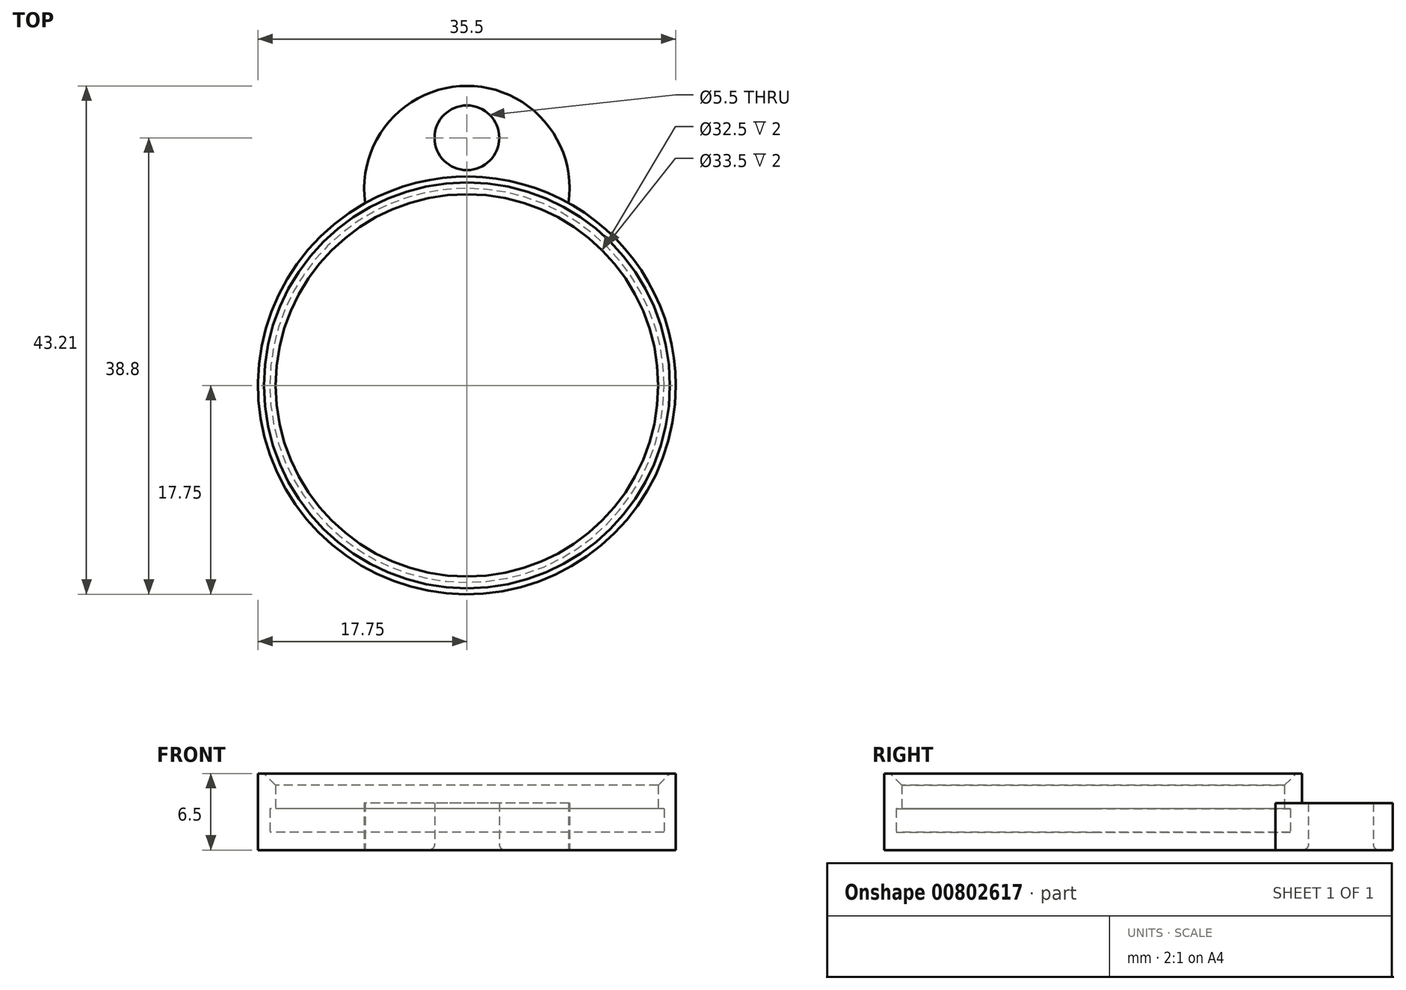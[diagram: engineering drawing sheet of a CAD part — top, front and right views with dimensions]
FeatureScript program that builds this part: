
annotation { "Feature Type Name" : "Feature", "Feature Type Description" : "" }
export const myFeature = defineFeature(function(context is Context, id is Id, definition is map)
    precondition{}
    {
        {
            var Q0;
            Q0=qCreatedBy(makeId("Top.planeOp"),FACE);
            var sketch = newSketch(context, id + "F0", { "sketchPlane" : qUnion([Q0])});
            skCircle(sketch, "E0", {"center": v(0, 0) * mm, "radius": 17.75 * mm});
            skLineSegment(sketch, "E1", {"start": v(-30.05, 0) * mm, "end": v(29.32, 0) * mm, "construction": true});
            skLineSegment(sketch, "E2", {"start": v(0, 26.58) * mm, "end": v(0, -26.58) * mm, "construction": true});
            skArc(sketch, "E3", {"start": v(0, 25.46) * mm, "mid": v(-6.6, 22.45) * mm, "end": v(-8.64, 15.5) * mm});
            skArc(sketch, "E4.MirrorCS", {"start": v(0, 25.46) * mm, "mid": v(6.6, 22.45) * mm, "end": v(8.64, 15.5) * mm});
            skCircle(sketch, "E5", {"center": v(0, 21.05) * mm, "radius": 2.75 * mm});
            skSolve(sketch);
        }
        {
            var Q0;
            {var subQ0=sQuery(id+"F0.wireOp",EDGE,"E0");var subQ1=makeQuery(id+"F0.imprint","INTERSECT",VERTEX,{"derivedFrom":[subQ0,sQuery(id+"F0.wireOp",EDGE,"E3")]});Q0=makeQuery(id+"F0.imprint","IMPRINT",FACE,{"disambiguationData":[TD([[makeQuery(id+"F0.imprint","IMPRINT",EDGE,{"disambiguationData":[TD([[subQ1,1.0]])],"derivedFrom":subQ0}),1.0]])]});}
            var Q1;
            {var subQ0=sQuery(id+"F0.wireOp",EDGE,"E3");Q1=makeQuery(id+"F0.imprint","IMPRINT",FACE,{"disambiguationData":[TD([[makeQuery(id+"F0.imprint","IMPRINT",EDGE,{"derivedFrom":subQ0}),1.0]])]});}
            extrude(context, id + "F1", {"entities" : qUnion([Q0, Q1]), "depth" : 1.5 * mm, "offsetDistance" : 25 * mm});
        }
        {
            var Q0;
            Q0=makeQuery(id+"F1.opExtrude","CAP_FACE",FACE,{"disambiguationData":[OSD([sQuery(id+"F0.wireOp",EDGE,"E0"),sQuery(id+"F0.wireOp",EDGE,"E3"),sQuery(id+"F0.wireOp",EDGE,"E4.MirrorCS"),sQuery(id+"F0.wireOp",EDGE,"E5")])],"isStart":false});
            var sketch = newSketch(context, id + "F2", { "sketchPlane" : qUnion([Q0])});
            skCircle(sketch, "E6", {"center": v(0, 0) * mm, "radius": 16.75 * mm});
            skCircle(sketch, "E7", {"center": v(0, 0) * mm, "radius": 17.75 * mm});
            skSolve(sketch);
        }
        {
            var Q0;
            Q0=makeQuery(id+"F2.imprint","IMPRINT",FACE,{"disambiguationData":[TD([[makeQuery(id+"F2.imprint","IMPRINT",EDGE,{"derivedFrom":sQuery(id+"F2.wireOp",EDGE,"E6")}),-1.0]])]});
            extrude(context, id + "F3", {"entities" : qUnion([Q0]), "operationType" : NewBodyOperationType.ADD, "depth" : 2 * mm, "offsetDistance" : 25 * mm});
        }
        {
            var Q0;
            {var subQ0=sQuery(id+"F0.wireOp",EDGE,"E0");var subQ1=sQuery(id+"F0.wireOp",EDGE,"E4.MirrorCS");var subQ2=sQuery(id+"F0.wireOp",EDGE,"E3");var subQ3=sQuery(id+"F0.wireOp",EDGE,"E5");Q0=makeQuery(id+"F3.boolean.opBoolean","SPLIT",FACE,{"disambiguationData":[TD([makeQuery(id+"F1.opExtrude","SWEPT_FACE",FACE,{"disambiguationData":[OSD([subQ0])]})])],"derivedFrom":makeQuery(id+"F1.opExtrude","CAP_FACE",FACE,{"disambiguationData":[OSD([subQ0,subQ2,subQ1,subQ3])],"isStart":false})});}
            var sketch = newSketch(context, id + "F4", { "sketchPlane" : qUnion([Q0])});
            skArc(sketch, "E8", {"start": v(8.64, 15.5) * mm, "mid": v(0, 25.49) * mm, "end": v(-8.64, 15.5) * mm});
            skSolve(sketch);
        }
        {
            var Q0;
            Q0=makeQuery(id+"F4.imprint","IMPRINT",FACE,{"disambiguationData":[TD([[makeQuery(id+"F4.imprint","IMPRINT",EDGE,{"derivedFrom":sQuery(id+"F4.wireOp",EDGE,"IEXGuXBA-ifSg-gj5B-lv7g-fZ8Ecxd1MQY6")}),-1.0]])]});
            var Q1;
            Q1=makeQuery(id+"F2.imprint","IMPRINT",FACE,{"disambiguationData":[TD([[makeQuery(id+"F2.imprint","IMPRINT",EDGE,{"derivedFrom":makeQuery(id+"F1.opExtrude","CAP_EDGE",EDGE,{"disambiguationData":[OSD([sQuery(id+"F0.wireOp",EDGE,"E5")])],"isStart":false})}),-1.0]])]});
            extrude(context, id + "F5", {"entities" : qUnion([Q0, Q1]), "operationType" : NewBodyOperationType.ADD, "depth" : 2.5 * mm, "offsetDistance" : 25 * mm});
        }
        {
            var Q0;
            Q0=makeQuery(id+"F3.opExtrude","CAP_FACE",FACE,{"disambiguationData":[OSD([sQuery(id+"F2.wireOp",EDGE,"E6"),sQuery(id+"F2.wireOp",EDGE,"E7")])],"isStart":false});
            var sketch = newSketch(context, id + "F6", { "sketchPlane" : qUnion([Q0])});
            skCircle(sketch, "E9", {"center": v(0, 0) * mm, "radius": 17.75 * mm});
            skCircle(sketch, "E10", {"center": v(0, 0) * mm, "radius": 16.25 * mm});
            skSolve(sketch);
        }
        {
            var Q0;
            Q0=makeQuery(id+"F6.imprint","IMPRINT",FACE,{"disambiguationData":[TD([[makeQuery(id+"F6.imprint","IMPRINT",EDGE,{"derivedFrom":makeQuery(id+"F3.opExtrude","CAP_EDGE",EDGE,{"disambiguationData":[OSD([sQuery(id+"F2.wireOp",EDGE,"E6")])],"isStart":false})}),-1.0]])]});
            var Q1;
            Q1=makeQuery(id+"F6.imprint","IMPRINT",FACE,{"disambiguationData":[TD([[makeQuery(id+"F6.imprint","IMPRINT",EDGE,{"derivedFrom":sQuery(id+"F6.wireOp",EDGE,"E10")}),-1.0]])]});
            extrude(context, id + "F7", {"entities" : qUnion([Q0, Q1]), "operationType" : NewBodyOperationType.ADD, "depth" : 3 * mm, "offsetDistance" : 25 * mm});
        }
        {
            var Q0;
            Q0=makeQuery(id+"F7.opExtrude","CAP_EDGE",EDGE,{"disambiguationData":[OSD([sQuery(id+"F6.wireOp",EDGE,"E10")])],"isStart":false});
            chamfer(context, id + "F8", {"entities" : qUnion([Q0]), "width" : 1 * mm, "tangentPropagation" : true});
        }
        {
            var Q0;
            Q0=makeQuery(id+"F1.opExtrude","CAP_EDGE",EDGE,{"disambiguationData":[OSD([sQuery(id+"F0.wireOp",EDGE,"E5")])],"isStart":true});
            fillet(context, id + "F9", {"entities" : qUnion([Q0]), "radius" : 0.5 * mm, "tangentPropagation" : true, "allowEdgeOverflow" : false});
        }
    });
